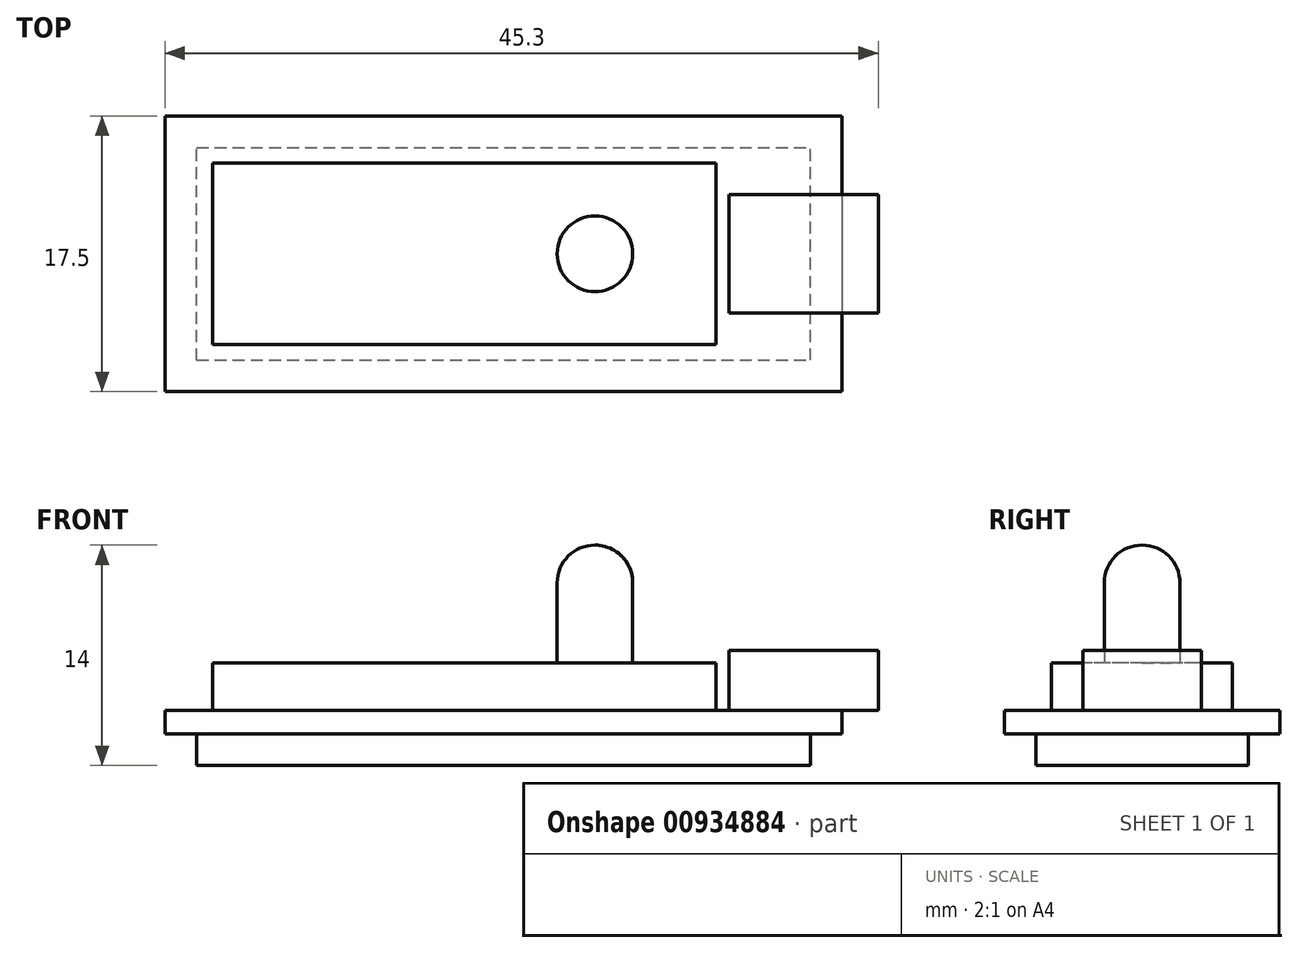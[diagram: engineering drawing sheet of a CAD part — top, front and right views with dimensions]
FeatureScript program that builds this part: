
annotation { "Feature Type Name" : "Feature", "Feature Type Description" : "" }
export const myFeature = defineFeature(function(context is Context, id is Id, definition is map)
    precondition{}
    {
        {
            var Q0;
            Q0=qCreatedBy(makeId("Top.planeOp"),FACE);
            var sketch = newSketch(context, id + "F0", { "sketchPlane" : qUnion([Q0])});
            skLineSegment(sketch, "E0.bottom", {"start": v(-21.5, 8.75) * mm, "end": v(21.5, 8.75) * mm});
            skLineSegment(sketch, "E0.top", {"start": v(-21.5, -8.75) * mm, "end": v(21.5, -8.75) * mm});
            skLineSegment(sketch, "E0.left", {"start": v(-21.5, 8.75) * mm, "end": v(-21.5, -8.75) * mm});
            skLineSegment(sketch, "E0.right", {"start": v(21.5, 8.75) * mm, "end": v(21.5, -8.75) * mm});
            skSolve(sketch);
        }
        {
            var Q0;
            Q0=qSketchRegion(id+"F0",true);
            extrude(context, id + "F1", {"entities" : qUnion([Q0]), "depth" : 1.5 * mm, "offsetDistance" : 25 * mm});
        }
        {
            var Q0;
            Q0=makeQuery(id+"F1.opExtrude","CAP_FACE",FACE,{"disambiguationData":[OSD([sQuery(id+"F0.wireOp",EDGE,"E0.bottom"),sQuery(id+"F0.wireOp",EDGE,"E0.top"),sQuery(id+"F0.wireOp",EDGE,"E0.left"),sQuery(id+"F0.wireOp",EDGE,"E0.right")])],"isStart":false});
            var sketch = newSketch(context, id + "F2", { "sketchPlane" : qUnion([Q0])});
            skLineSegment(sketch, "E1.bottom", {"start": v(14.3, 3.75) * mm, "end": v(23.8, 3.75) * mm});
            skLineSegment(sketch, "E1.top", {"start": v(14.3, -3.75) * mm, "end": v(23.8, -3.75) * mm});
            skLineSegment(sketch, "E1.left", {"start": v(14.3, 3.75) * mm, "end": v(14.3, -3.75) * mm});
            skLineSegment(sketch, "E1.right", {"start": v(23.8, 3.75) * mm, "end": v(23.8, -3.75) * mm});
            skSolve(sketch);
        }
        {
            var Q0;
            Q0=qSketchRegion(id+"F2",true);
            extrude(context, id + "F3", {"entities" : qUnion([Q0]), "operationType" : NewBodyOperationType.ADD, "depth" : 3.8 * mm, "offsetDistance" : 25 * mm});
        }
        {
            var Q0;
            Q0=makeQuery(id+"F1.opExtrude","CAP_FACE",FACE,{"disambiguationData":[OSD([sQuery(id+"F0.wireOp",EDGE,"E0.bottom"),sQuery(id+"F0.wireOp",EDGE,"E0.top"),sQuery(id+"F0.wireOp",EDGE,"E0.left"),sQuery(id+"F0.wireOp",EDGE,"E0.right")])],"isStart":false});
            var sketch = newSketch(context, id + "F4", { "sketchPlane" : qUnion([Q0])});
            skLineSegment(sketch, "E2.bottom", {"start": v(-18.5, 5.75) * mm, "end": v(13.5, 5.75) * mm});
            skLineSegment(sketch, "E2.top", {"start": v(-18.5, -5.75) * mm, "end": v(13.5, -5.75) * mm});
            skLineSegment(sketch, "E2.left", {"start": v(-18.5, 5.75) * mm, "end": v(-18.5, -5.75) * mm});
            skLineSegment(sketch, "E2.right", {"start": v(13.5, 5.75) * mm, "end": v(13.5, -5.75) * mm});
            skSolve(sketch);
        }
        {
            var Q0;
            Q0=makeQuery(id+"F4.imprint","IMPRINT",FACE,{"disambiguationData":[TD([[makeQuery(id+"F4.imprint","IMPRINT",EDGE,{"derivedFrom":sQuery(id+"F4.wireOp",EDGE,"E2.bottom")}),-1.0]])]});
            extrude(context, id + "F5", {"entities" : qUnion([Q0]), "operationType" : NewBodyOperationType.ADD, "depth" : 3 * mm, "offsetDistance" : 25 * mm});
        }
        {
            var Q0;
            Q0=makeQuery(id+"F1.opExtrude","CAP_FACE",FACE,{"disambiguationData":[OSD([sQuery(id+"F0.wireOp",EDGE,"E0.bottom"),sQuery(id+"F0.wireOp",EDGE,"E0.top"),sQuery(id+"F0.wireOp",EDGE,"E0.left"),sQuery(id+"F0.wireOp",EDGE,"E0.right")])],"isStart":true});
            var sketch = newSketch(context, id + "F6", { "sketchPlane" : qUnion([Q0])});
            skLineSegment(sketch, "E3.bottom", {"start": v(-19.5, 6.75) * mm, "end": v(19.5, 6.75) * mm});
            skLineSegment(sketch, "E3.top", {"start": v(-19.5, -6.75) * mm, "end": v(19.5, -6.75) * mm});
            skLineSegment(sketch, "E3.left", {"start": v(-19.5, 6.75) * mm, "end": v(-19.5, -6.75) * mm});
            skLineSegment(sketch, "E3.right", {"start": v(19.5, 6.75) * mm, "end": v(19.5, -6.75) * mm});
            skSolve(sketch);
        }
        {
            var Q0;
            Q0=makeQuery(id+"F6.imprint","IMPRINT",FACE,{"disambiguationData":[TD([[makeQuery(id+"F6.imprint","IMPRINT",EDGE,{"derivedFrom":sQuery(id+"F6.wireOp",EDGE,"E3.bottom")}),-1.0]])]});
            extrude(context, id + "F7", {"entities" : qUnion([Q0]), "operationType" : NewBodyOperationType.ADD, "depth" : 2 * mm, "offsetDistance" : 25 * mm});
        }
        {
            var Q0;
            Q0=makeQuery(id+"F5.opExtrude","CAP_FACE",FACE,{"disambiguationData":[OSD([sQuery(id+"F4.wireOp",EDGE,"E2.bottom"),sQuery(id+"F4.wireOp",EDGE,"E2.top"),sQuery(id+"F4.wireOp",EDGE,"E2.left"),sQuery(id+"F4.wireOp",EDGE,"E2.right")])],"isStart":false});
            var sketch = newSketch(context, id + "F8", { "sketchPlane" : qUnion([Q0])});
            skCircle(sketch, "E4", {"center": v(5.8, 0) * mm, "radius": 2.4 * mm});
            skSolve(sketch);
        }
        {
            var Q0;
            Q0=makeQuery(id+"F8.imprint","IMPRINT",FACE,{"disambiguationData":[TD([[makeQuery(id+"F8.imprint","IMPRINT",EDGE,{"derivedFrom":sQuery(id+"F8.wireOp",EDGE,"E4")}),1.0]])]});
            extrude(context, id + "F9", {"entities" : qUnion([Q0]), "operationType" : NewBodyOperationType.ADD, "depth" : 7.5 * mm, "offsetDistance" : 25 * mm});
        }
        {
            var Q0;
            Q0=makeQuery(id+"F9.opExtrude","CAP_EDGE",EDGE,{"disambiguationData":[OSD([sQuery(id+"F8.wireOp",EDGE,"E4")])],"isStart":false});
            fillet(context, id + "F10", {"entities" : qUnion([Q0]), "radius" : 2.4 * mm, "tangentPropagation" : true, "allowEdgeOverflow" : false});
        }
    });
